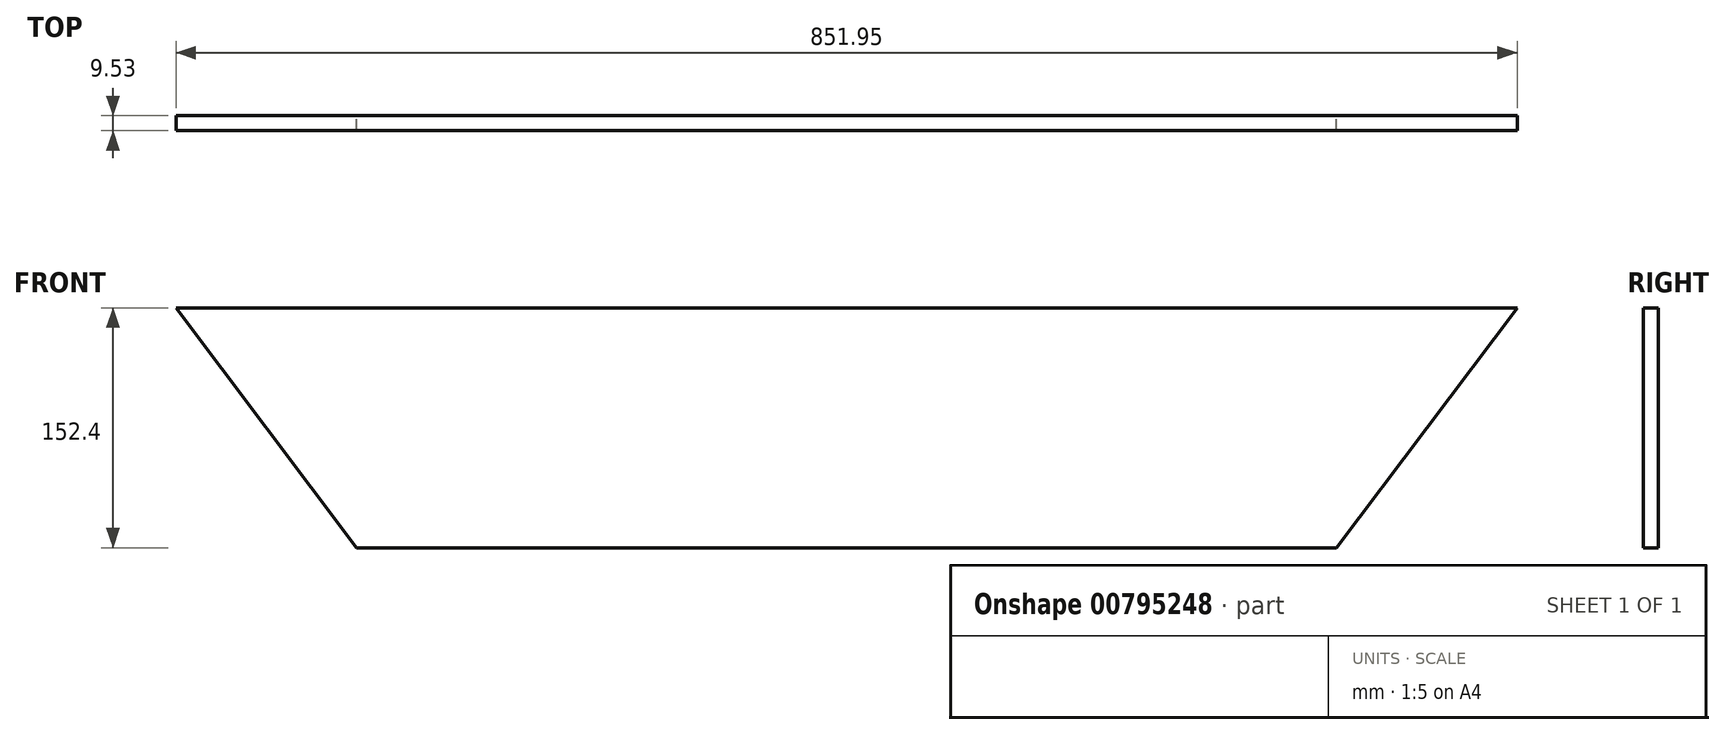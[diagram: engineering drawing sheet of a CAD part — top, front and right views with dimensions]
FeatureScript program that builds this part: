
annotation { "Feature Type Name" : "Feature", "Feature Type Description" : "" }
export const myFeature = defineFeature(function(context is Context, id is Id, definition is map)
    precondition{}
    {
        {
            var Q0;
            Q0=qCreatedBy(makeId("Front.planeOp"),FACE);
            var sketch = newSketch(context, id + "F0", { "sketchPlane" : qUnion([Q0])});
            skLineSegment(sketch, "E0", {"start": v(-443.5, 93.52) * mm, "end": v(-328.67, -58.88) * mm});
            skLineSegment(sketch, "E1", {"start": v(-328.67, -58.88) * mm, "end": v(293.63, -58.88) * mm});
            skLineSegment(sketch, "E2", {"start": v(293.63, -58.88) * mm, "end": v(408.45, 93.52) * mm});
            skLineSegment(sketch, "E3", {"start": v(408.45, 93.52) * mm, "end": v(-443.5, 93.52) * mm});
            skSolve(sketch);
        }
        {
            var Q0;
            Q0 = qSketchRegion(id + "F0", true);
            extrude(context, id + "F1", {"entities" : qUnion([Q0]), "depth" : 9.52 * mm, "offsetDistance" : 25.4 * mm});
        }
    });
